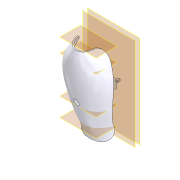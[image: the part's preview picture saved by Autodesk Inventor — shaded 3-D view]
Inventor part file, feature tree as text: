
AUTODESK INVENTOR PART (.ipt)
format: ipt  version: 2020.2 (Build 242310000, 310)  size: 370,688 bytes
history: native  units: mm
features: sketch x8, plane x6, extrude x3, loft x1, shell x1, fillet x1
ambient origin geometry x8: Origin, YZ Plane, XZ Plane, XY Plane, X Axis, Y Axis, Z Axis, Center Point
bodies: Solid1 (feature_tree)
feature tree (20):
  sketch  "Sketch1"  dims[d0=35.0mm d3=15.0mm d4=17.5mm d5=17.5mm]
  plane  "Work Plane2"
  sketch  "Sketch3"  dims[d7=20.0mm d8=5.0mm]
  plane  "Work Plane3"
  sketch  "Sketch4"  dims[d9=21.0mm d10=20.0mm]
  plane  "Work Plane4"
  plane  "Work Plane5"
  sketch  "Sketch5"  dims[d12=40.0mm d13=5.0mm]
  sketch  "Sketch7"  dims[d15=20.0mm]
  loft  "Loft2"
  shell  "Shell2"  Thickness=17.5mm
  fillet  "Fillet2"  Radius=17.5mm
  plane  "Work Plane6"
  extrude  "Extrusion3"  Depth=5.0mm
  plane  "Work Plane7"
  extrude  "Extrusion4"  Depth=20.0mm
  extrude  "Extrusion5"  Depth=5.0mm
  sketch  "Sketch8"  dims[d16=20.0mm]
  sketch  "Sketch9"  dims[d17=5.0mm]
  sketch  "Sketch10"  dims[d18=5.0mm d20=5.0mm d38=15.0mm d39=8.0mm d40=12.0mm d43=10.0mm d44=90.0deg d45=0.0mm d46=90.0deg d47=0.0mm d48=90.0deg d49=0.0mm d50=90.0deg d51=0.0mm d52=90.0deg d53=1.0mm d54=10.0mm d57=-16.0mm d58=9.0mm d59=9.0mm d60=3.0mm d61=52.761mm d62=0.0mm d63=5.0mm d64=6.0mm d65=47.761mm d66=0.0mm d67=0.2mm d68=2.0mm d69=2.0mm d70=3.0mm d71=0.2mm d72=2.0mm d73=2.0mm d74=3.0mm d75=2.0mm d76=0.0mm]
